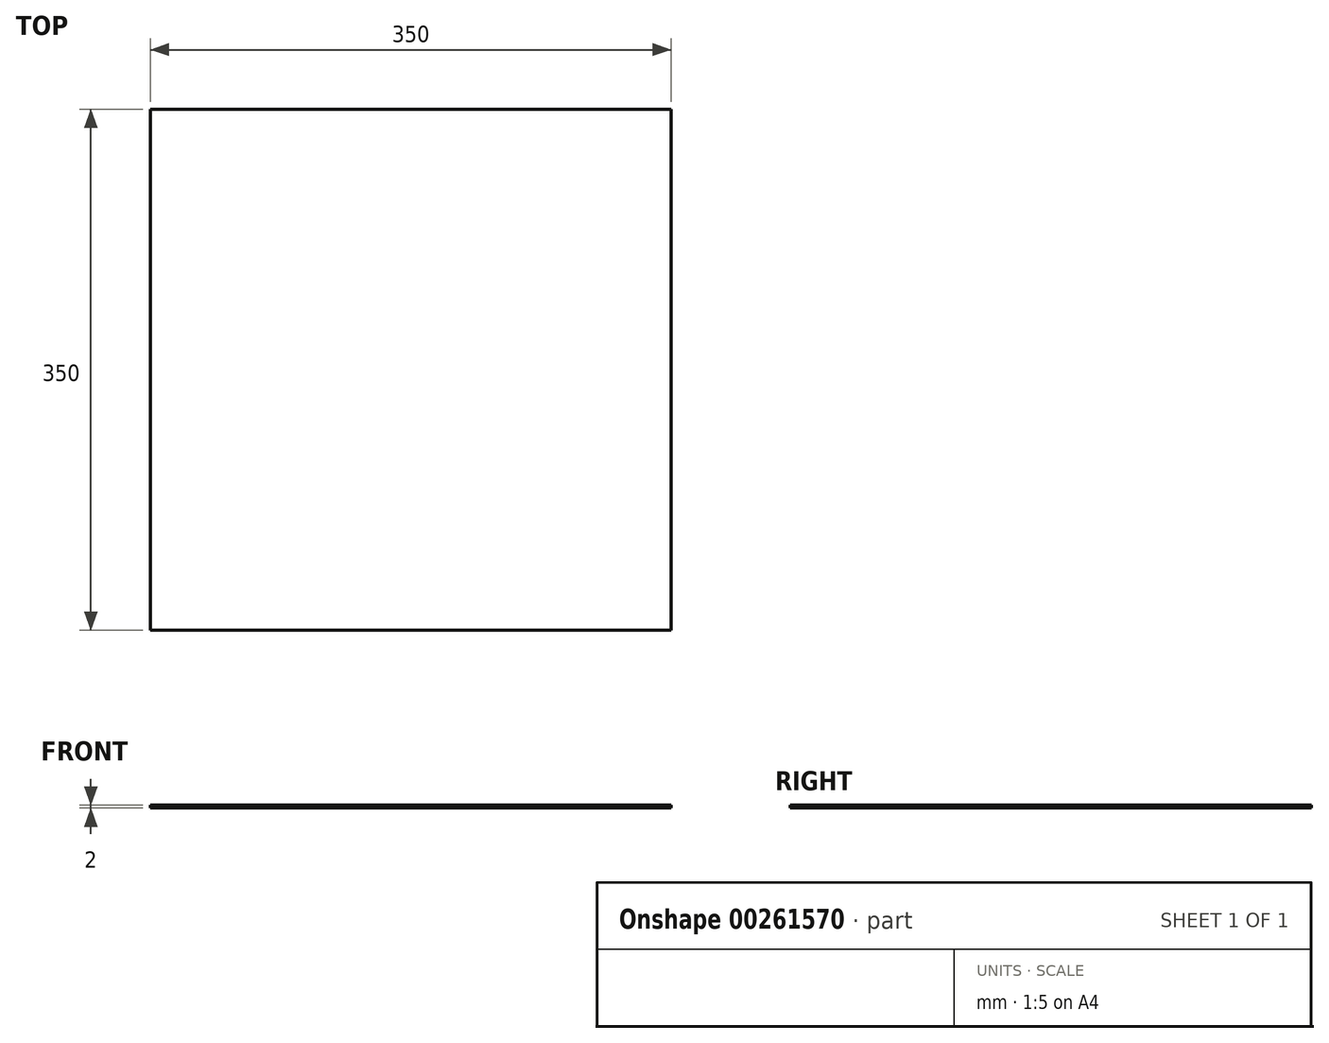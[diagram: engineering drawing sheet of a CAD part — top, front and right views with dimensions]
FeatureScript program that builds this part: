
annotation { "Feature Type Name" : "Feature", "Feature Type Description" : "" }
export const myFeature = defineFeature(function(context is Context, id is Id, definition is map)
    precondition{}
    {
        {
            var Q0;
            Q0=qCreatedBy(makeId("Top.planeOp"),FACE);
            var sketch = newSketch(context, id + "F0", { "sketchPlane" : qUnion([Q0])});
            skLineSegment(sketch, "E0.bottom", {"start": v(178.35, -175) * mm, "end": v(-171.65, -175) * mm});
            skLineSegment(sketch, "E0.top", {"start": v(178.35, 175) * mm, "end": v(-171.65, 175) * mm});
            skLineSegment(sketch, "E0.left", {"start": v(178.35, -175) * mm, "end": v(178.35, 175) * mm});
            skLineSegment(sketch, "E0.right", {"start": v(-171.65, -175) * mm, "end": v(-171.65, 175) * mm});
            skPoint(sketch, "E0.middle", {"position": v(3.35, 0) * mm});
            skSolve(sketch);
        }
        {
            var Q0;
            Q0=qSketchRegion(id+"F0",true);
            extrude(context, id + "F1", {"entities" : qUnion([Q0]), "depth" : 2 * mm});
        }
    });
